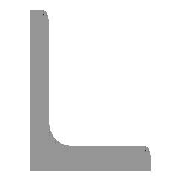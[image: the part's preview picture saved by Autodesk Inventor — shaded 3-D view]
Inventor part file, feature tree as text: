
AUTODESK INVENTOR PART (.ipt)
format: ipt  version: 2013 (Build 170138000, 138)  size: 129,536 bytes
history: native  units: mm (DEFAULTED — no unit token found)
features: other x4, plane x3, split x2, sketch x2
ambient origin geometry x8: Origin, YZ Plane, XZ Plane, XY Plane, X Axis, Y Axis, Z Axis, Center Point
bodies: Solid1 (feature_tree), Body (feature_tree)
feature tree (11):
  parser-record x1  (decoder bookkeeping rows leaked as tree rows — omitted from the tree; the rows remain in map.json)
  other  "Driven Length"
  other  "Start plane"
  other  "End plane"
  plane  "Work Plane4"
  split  "Split1"
  plane  "Work Plane5"
  split  "Split2"
  sketch  "Sketch3"  dims[d0=38.1mm]
  plane  "Work Plane3"
  sketch  "Sketch4"  dims[d1=38.1mm d2=4.7625mm d3=4.7625mm d4=1066.8mm d5=0.0mm d10=0.0mm d11=0.0mm d12=-0.0mm d13=1066.8mm d14=4.826mm d15=2.286mm d16=90.0deg d17=1066.8mm]
